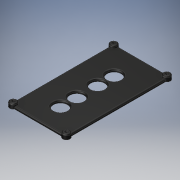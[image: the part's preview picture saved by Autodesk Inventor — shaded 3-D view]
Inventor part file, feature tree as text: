
AUTODESK INVENTOR PART (.ipt)
format: ipt  version: 2017 (Build 210142000, 142)  size: 209,920 bytes
history: native  units: in
note: dims shown in document units (in); Inventor stores cm internally (conversion verified against a paired STEP export)
features: hole x4, reference x4, extrude x3, fillet x3, sketch x3, other x3, projected_geometry x1
ambient origin geometry x8: Origin, YZ Plane, XZ Plane, XY Plane, X Axis, Y Axis, Z Axis, Center Point
bodies: Solid1 (feature_tree)
feature tree (21):
  extrude  "Extrusion1"  Depth=5.5in
  extrude  "Extrusion2"  Depth=0.375in
  fillet  "Fillet1"  Radius=0.375in
  hole  "Hole1"  [1 undecoded]
  hole  "Hole2"  [1 undecoded]
  hole  "Hole3"  [1 undecoded]
  hole  "Hole4"  [1 undecoded]
  extrude  "Extrusion5"  Depth=0.0625in
  fillet  "Fillet2"  Radius=0.094in
  fillet  "Fillet3"  Radius=0.094in
  sketch  "Sketch1"  dims[d0=3.0in d1=5.5in]
  sketch  "Sketch2"  dims[d2=0.125in d3=0.0in d4=0.375in d5=0.375in]
  projected_geometry  "Projected Loop1"
  sketch  "Sketch5"  dims[d6=0.375in d7=0.375in d8=0.094in d9=0.094in d10=0.094in d11=0.094in d12=0.094in d13=0.094in d14=0.094in d15=0.094in d16=0.25in d17=0.0in d18=0.0625in d19=1.0in d20=1.0in d21=0.096in d22=0.75in d23=0.172in d24=0.25in d25=0.5635in d26=1.0in d27=0.0in d28=1.0in d29=1.0in d30=0.096in d31=0.75in d32=0.172in d33=0.25in d34=0.5635in d35=1.0in d36=0.0in d37=1.0in d38=1.0in d39=0.096in d40=0.75in d41=0.172in d42=0.25in d43=0.5635in d44=1.0in d45=0.0in d46=1.0in d47=1.0in d48=0.096in d49=0.75in d50=0.172in d51=0.25in d52=0.5635in d53=1.0in d54=0.0in d67=0.02in d68=0.02in d69=0.02in d70=0.02in d71=0.25in d72=0.0in d73=0.0625in d74=0.0625in]
  reference  "Reference9"
  reference  "Reference10"
  reference  "Reference11"
  reference  "Reference12"
  parser-record x1  (decoder bookkeeping rows leaked as tree rows — omitted from the tree; the rows remain in map.json)
  other  "main_assy.iam"
  other  "PCB:1"
note: 4 required parameter values undecoded (feature->parameter linkage not recoverable at this tier; creation-order binding heuristic only, values carry confidence <= 0.55)
note: 1 file-system path scrubbed to <path> (originals preserved in map.json)
